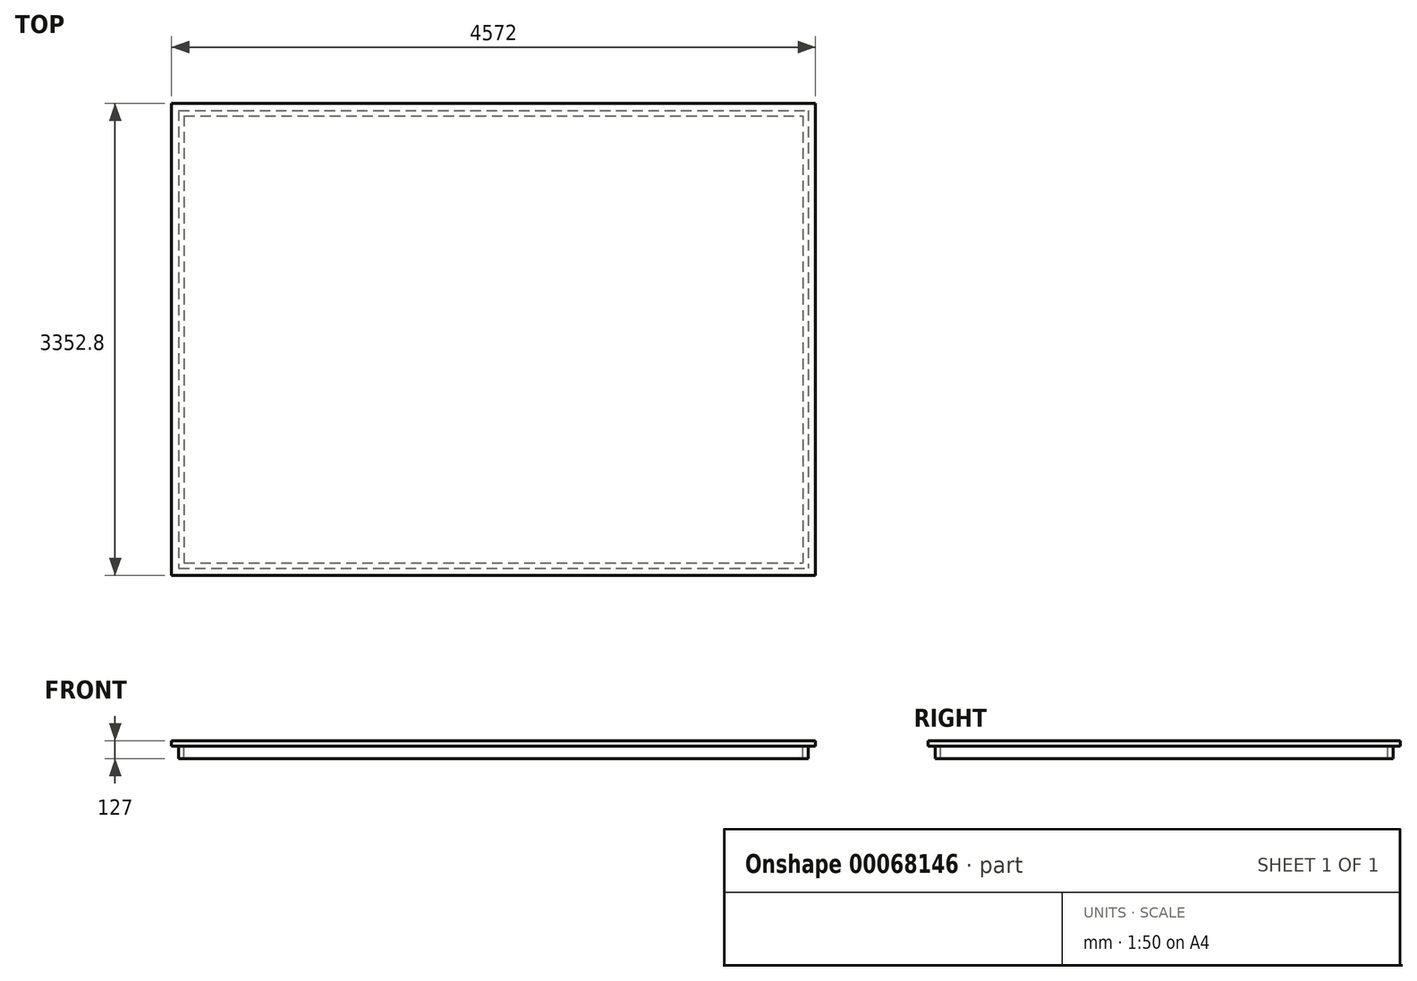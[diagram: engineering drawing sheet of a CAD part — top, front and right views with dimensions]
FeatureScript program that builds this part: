
annotation { "Feature Type Name" : "Feature", "Feature Type Description" : "" }
export const myFeature = defineFeature(function(context is Context, id is Id, definition is map)
    precondition{}
    {
        {
            var Q0;
            Q0=qCreatedBy(makeId("Top.planeOp"),FACE);
            var sketch = newSketch(context, id + "F0", { "sketchPlane" : qUnion([Q0])});
            skLineSegment(sketch, "E0.bottom", {"start": v(-2027.1, 1969.6) * mm, "end": v(2544.9, 1969.6) * mm});
            skLineSegment(sketch, "E0.top", {"start": v(-2027.1, -1383.2) * mm, "end": v(2544.9, -1383.2) * mm});
            skLineSegment(sketch, "E0.left", {"start": v(-2027.1, 1969.6) * mm, "end": v(-2027.1, -1383.2) * mm});
            skLineSegment(sketch, "E0.right", {"start": v(2544.9, 1969.6) * mm, "end": v(2544.9, -1383.2) * mm});
            skSolve(sketch);
        }
        {
            var Q0;
            Q0 = qSketchRegion(id + "F0", true);
            extrude(context, id + "F1", {"entities" : qUnion([Q0]), "depth" : 38.1 * mm});
        }
        {
            var Q0;
            Q0=makeQuery(id+"F1.opExtrude","CAP_FACE",FACE,{"disambiguationData":[OSD([sQuery(id+"F0.wireOp",EDGE,"E0.bottom"),sQuery(id+"F0.wireOp",EDGE,"E0.top"),sQuery(id+"F0.wireOp",EDGE,"E0.left"),sQuery(id+"F0.wireOp",EDGE,"E0.right")])],"isStart":true});
            var sketch = newSketch(context, id + "F2", { "sketchPlane" : qUnion([Q0])});
            skLineSegment(sketch, "E1.0", {"start": v(-1976.3, 1332.4) * mm, "end": v(2494.1, 1332.4) * mm});
            skLineSegment(sketch, "E1.1", {"start": v(-1976.3, -1918.8) * mm, "end": v(-1976.3, 1332.4) * mm});
            skLineSegment(sketch, "E1.2", {"start": v(-1976.3, -1918.8) * mm, "end": v(2494.1, -1918.8) * mm});
            skLineSegment(sketch, "E1.3", {"start": v(2494.1, -1918.8) * mm, "end": v(2494.1, 1332.4) * mm});
            skLineSegment(sketch, "E2.0", {"start": v(-1938.2, 1294.3) * mm, "end": v(2456, 1294.3) * mm});
            skLineSegment(sketch, "E2.1", {"start": v(-1938.2, -1880.7) * mm, "end": v(-1938.2, 1294.3) * mm});
            skLineSegment(sketch, "E2.2", {"start": v(-1938.2, -1880.7) * mm, "end": v(2456, -1880.7) * mm});
            skLineSegment(sketch, "E2.3", {"start": v(2456, -1880.7) * mm, "end": v(2456, 1294.3) * mm});
            skSolve(sketch);
        }
        {
            var Q0;
            Q0 = qSketchRegion(id + "F2", true);
            extrude(context, id + "F3", {"entities" : qUnion([Q0]), "operationType" : NewBodyOperationType.ADD, "depth" : 88.9 * mm});
        }
    });
